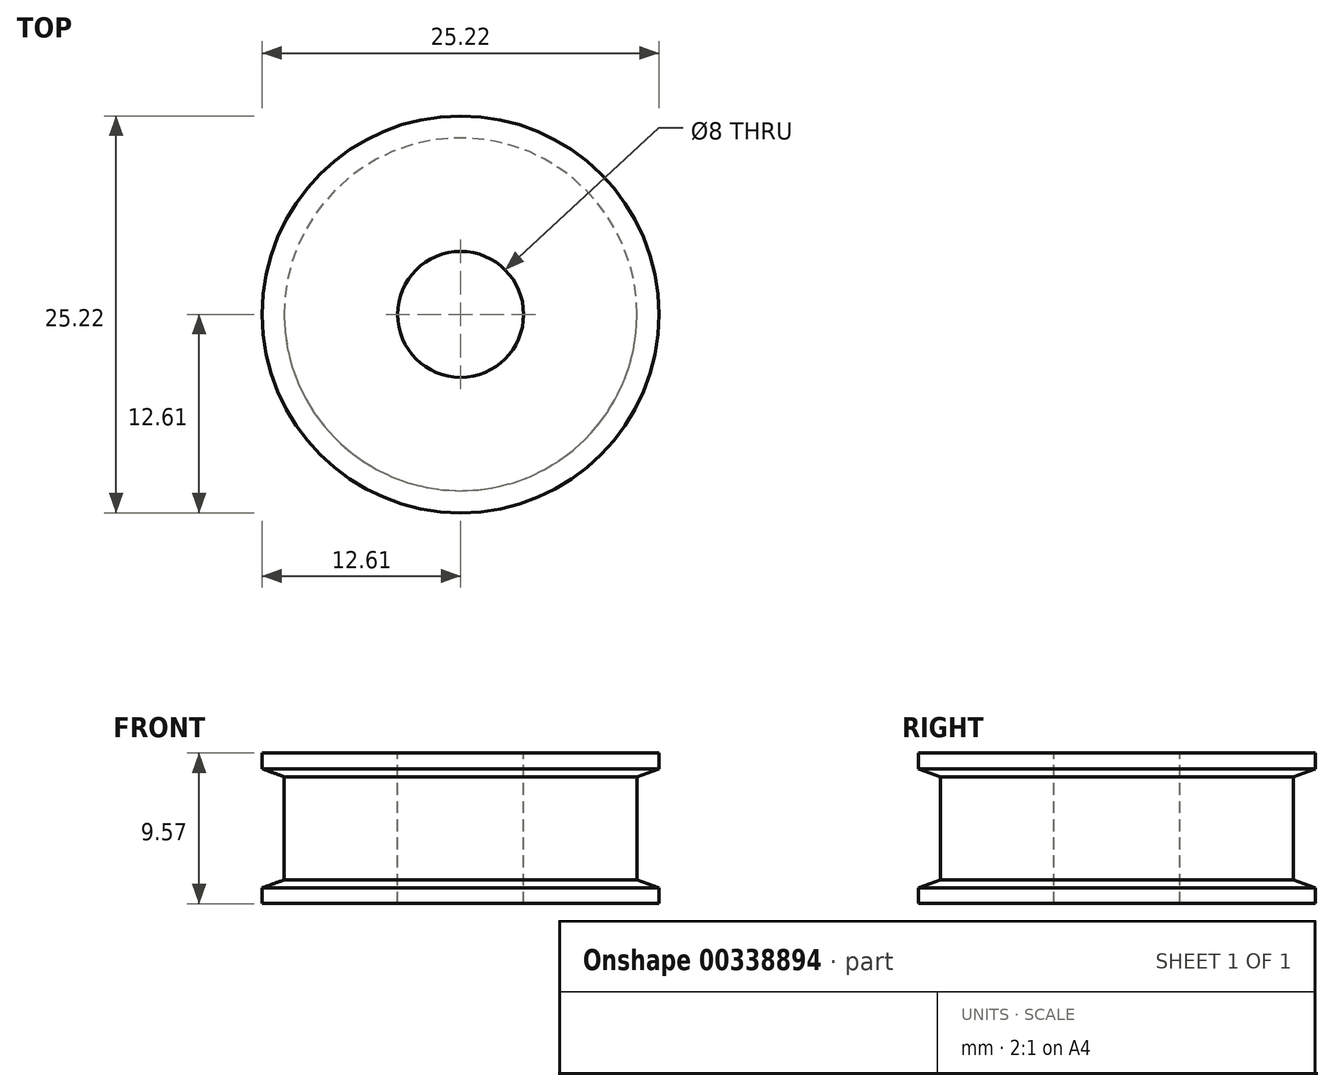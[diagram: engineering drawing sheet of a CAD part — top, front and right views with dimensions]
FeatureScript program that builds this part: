
annotation { "Feature Type Name" : "Feature", "Feature Type Description" : "" }
export const myFeature = defineFeature(function(context is Context, id is Id, definition is map)
    precondition{}
    {
        {
            assignVariable(context, id + "F0", {"name" : "teeth", "anyValue" : 36});
        }
        {
            assignVariable(context, id + "F1", {"name" : "total_length", "anyValue" : 9});
        }
        {
            var Q0;
            Q0=qCreatedBy(makeId("Top.planeOp"),FACE);
            var sketch = newSketch(context, id + "F2", { "sketchPlane" : qUnion([Q0])});
            skLineSegment(sketch, "E0", {"start": v(0, 0) * mm, "end": v(0, 10.46) * mm, "construction": true});
            skCircle(sketch, "E1", {"center": v(0, 0) * mm, "radius": 11.2 * mm});
            skPoint(sketch, "E2.MirrorCS.end.orphan", {"position": v(0.98, 11.16) * mm});
            skLineSegment(sketch, "E3", {"start": v(0.98, 11.16) * mm, "end": v(1, 11.42) * mm, "construction": true});
            skLineSegment(sketch, "E4", {"start": v(-0.98, 11.16) * mm, "end": v(-1, 11.42) * mm, "construction": true});
            skLineSegment(sketch, "E5", {"start": v(0, 10.46) * mm, "end": v(0, 11.2) * mm, "construction": true});
            skLineSegment(sketch, "E6", {"start": v(0, 11.2) * mm, "end": v(0, 11.46) * mm, "construction": true});
            skArc(sketch, "E7", {"start": v(1, 11.42) * mm, "mid": v(0, 11.46) * mm, "end": v(-1, 11.42) * mm, "construction": true});
            skLineSegment(sketch, "E8", {"start": v(0.98, 11.16) * mm, "end": v(0.91, 10.42) * mm});
            skLineSegment(sketch, "E9", {"start": v(0.91, 10.42) * mm, "end": v(0, 0) * mm});
            skLineSegment(sketch, "E10", {"start": v(0, 0) * mm, "end": v(-0.91, 10.42) * mm});
            skLineSegment(sketch, "E11", {"start": v(-0.91, 10.42) * mm, "end": v(-0.98, 11.16) * mm});
            skArc(sketch, "E12", {"start": v(0, 11.2) * mm, "mid": v(-0.2, 11.2) * mm, "end": v(-0.4, 11.2) * mm});
            skArc(sketch, "E13", {"start": v(0.91, 10.42) * mm, "mid": v(0, 10.46) * mm, "end": v(-0.91, 10.42) * mm, "construction": true});
            skLineSegment(sketch, "E14", {"start": v(1, 11.42) * mm, "end": v(1.03, 11.8) * mm, "construction": true});
            skLineSegment(sketch, "E15", {"start": v(-1, 11.42) * mm, "end": v(-1.03, 11.8) * mm, "construction": true});
            skArc(sketch, "E16", {"start": v(-1.03, 11.8) * mm, "mid": v(0, 11.84) * mm, "end": v(1.03, 11.8) * mm, "construction": true});
            skArc(sketch, "E17", {"start": v(-0.98, 11.16) * mm, "mid": v(0.49, -11.2) * mm, "end": v(0, 11.2) * mm});
            skSolve(sketch);
        }
        {
            var Q0;
            Q0=makeQuery(id+"F2.imprint","IMPRINT",FACE,{"disambiguationData":[TD([[makeQuery(id+"F2.imprint","IMPRINT",EDGE,{"derivedFrom":sQuery(id+"F2.wireOp",EDGE,"P1uhFWbC-AUpd-SlUc-z3bf-78FxmXMfxVC7")}),-1.0]])]});
            var Q1;
            {var subQ1=sQuery(id+"F2.wireOp",EDGE,"E11");Q1=makeQuery(id+"F2.imprint","IMPRINT",FACE,{"disambiguationData":[TD([[makeQuery(id+"F2.imprint","IMPRINT",EDGE,{"derivedFrom":subQ1}),-1.0]])]});}
            var Q2;
            {var subQ0=sQuery(id+"F2.wireOp",EDGE,"E9");Q2=makeQuery(id+"F2.imprint","IMPRINT",FACE,{"disambiguationData":[TD([[makeQuery(id+"F2.imprint","IMPRINT",EDGE,{"derivedFrom":subQ0}),-1.0]])]});}
            extrude(context, id + "F3", {"entities" : qUnion([Q0, Q1, Q2]), "endBound" : BoundingType.SYMMETRIC, "depth" : (getVariable(context, 'total_length')) * mm});
        }
        {
            var Q0;
            Q0=makeQuery(id+"F3.opExtrude","SWEPT_BODY",BODY,{"disambiguationData":[OSD([sQuery(id+"F2.wireOp",EDGE,"E1"),sQuery(id+"F2.wireOp",EDGE,"P1uhFWbC-AUpd-SlUc-z3bf-78FxmXMfxVC7"),sQuery(id+"F2.wireOp",EDGE,"E8"),sQuery(id+"F2.wireOp",EDGE,"E9"),sQuery(id+"F2.wireOp",EDGE,"E10"),sQuery(id+"F2.wireOp",EDGE,"E11"),sQuery(id+"F2.wireOp",EDGE,"aZysBSW6-xeYk-Y5AL-URpO-NHl3PhOeUQth"),sQuery(id+"F2.wireOp",EDGE,"Rlz8ElYD-njMK-K2Gw-WVJm-wIMkdtHgt6w2"),sQuery(id+"F2.wireOp",EDGE,"dd8ef0db-efd4-4436-b532-5508418b62120.MirrorCS"),sQuery(id+"F2.wireOp",EDGE,"e644996f-e673-4261-af5f-634a3a17fb890.MirrorCS"),sQuery(id+"F2.wireOp",EDGE,"3e81cde9-3123-4241-844a-bf780b0a6bc10.MirrorCS")])]});
            var Q1;
            Q1=makeQuery(id+"F3.opExtrude","SWEPT_EDGE",EDGE,{"disambiguationData":[OSD([sQuery(id+"F2.wireOp",EDGE,"E9"),sQuery(id+"F2.wireOp",EDGE,"E10")])]});
            circularPattern(context, id + "F4", {"operationType" : NewBodyOperationType.ADD, "entities" : qUnion([Q0]), "axis" : qUnion([Q1]), "angle" : 360 * degree, "instanceCount" : getVariable(context, 'teeth'), "equalSpace" : true});
        }
        {
            var Q0;
            Q0=qCreatedBy(makeId("Front.planeOp"),FACE);
            var sketch = newSketch(context, id + "F5", { "sketchPlane" : qUnion([Q0])});
            skLineSegment(sketch, "E18", {"start": v(0, 4.5) * mm, "end": v(12.6, 4.5) * mm});
            skLineSegment(sketch, "E19", {"start": v(12.6, 4.5) * mm, "end": v(12.6, 3.5) * mm});
            skLineSegment(sketch, "E20", {"start": v(12.6, 3.5) * mm, "end": v(10.46, 2.72) * mm});
            skLineSegment(sketch, "E21", {"start": v(10.46, 2.72) * mm, "end": v(0, 2.72) * mm});
            skLineSegment(sketch, "E22", {"start": v(0, 2.72) * mm, "end": v(0, 4.5) * mm});
            skLineSegment(sketch, "E23", {"start": v(0, -3.28) * mm, "end": v(10.46, -3.28) * mm});
            skLineSegment(sketch, "E24", {"start": v(10.46, -3.28) * mm, "end": v(12.6, -4.07) * mm});
            skLineSegment(sketch, "E25", {"start": v(12.6, -4.07) * mm, "end": v(12.6, -5.07) * mm});
            skLineSegment(sketch, "E26", {"start": v(12.6, -5.07) * mm, "end": v(0, -5.07) * mm});
            skLineSegment(sketch, "E27", {"start": v(0, -5.07) * mm, "end": v(0, -3.28) * mm});
            skSolve(sketch);
        }
        {
            var Q0;
            Q0=qSketchRegion(id+"F5",true);
            var Q1;
            Q1=sQuery(id+"F5.wireOp",EDGE,"E22");
            revolve(context, id + "F6", {"operationType" : NewBodyOperationType.ADD, "entities" : qUnion([Q0]), "axis" : qUnion([Q1]), "revolveType" : RevolveType.FULL});
        }
        {
            var Q0;
            Q0=qCreatedBy(makeId("Top.planeOp"),FACE);
            var sketch = newSketch(context, id + "F7", { "sketchPlane" : qUnion([Q0])});
            skCircle(sketch, "E28", {"center": v(0, 0) * mm, "radius": 4 * mm});
            skSolve(sketch);
        }
        {
            var Q0;
            Q0=qSketchRegion(id+"F7",true);
            extrude(context, id + "F8", {"entities" : qUnion([Q0]), "operationType" : NewBodyOperationType.REMOVE, "endBound" : BoundingType.SYMMETRIC, "oppositeDirection" : true, "depth" : 100 * mm});
        }
    });
